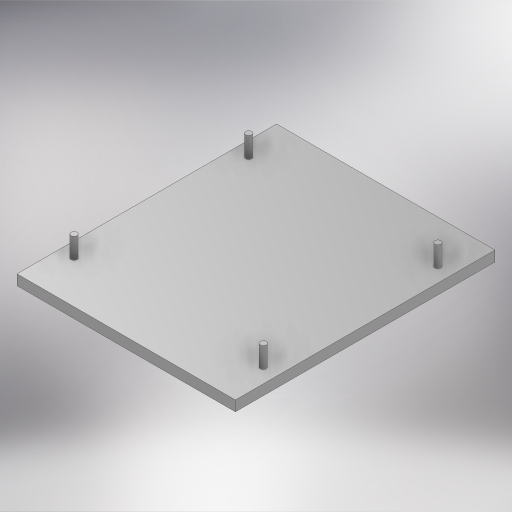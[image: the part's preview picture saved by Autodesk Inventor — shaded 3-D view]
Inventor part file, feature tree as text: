
AUTODESK INVENTOR PART (.ipt)
format: ipt  version: 2024 (Build 280153000, 153)  size: 340,480 bytes
history: native  units: mm
features: other x11, extrude x3, sketch x3
ambient origin geometry x8: Origin, YZ Plane, XZ Plane, XY Plane, X Axis, Y Axis, Z Axis, Center Point
bodies: Body1 (feature_tree)
feature tree (17):
  other  "Sólido1"
  extrude  "Extrusión1"  Depth=126.0mm
  extrude  "Extrusión2"  Depth=53.0mm
  extrude  "Extrusión3"  Depth=3.0mm
  sketch  "Boceto1"  dims[d1=106.0mm d2=126.0mm]
  sketch  "Boceto2"  dims[d3=53.0mm d4=63.0mm]
  sketch  "Boceto3"  dims[d5=5.0mm d6=0.0mm d7=3.0mm d8=20.616mm d9=7.071mm d10=10.0mm d11=0.0mm d12=52.5mm d13=126.0mm d14=106.0mm d15=52.5mm d16=35.0mm d17=35.0mm d18=35.0mm d19=35.0mm d20=35.0mm d21=2.0mm d22=0.0mm]
  other  "Finish1"
  other  "Finish2"
  other  "Finish3"
  other  "Finish4"
  other  "Finish5"
  other  "Finish6"
  other  "Finish7"
  other  "Finish8"
  other  "Finish9"
  other  "Finish10"
